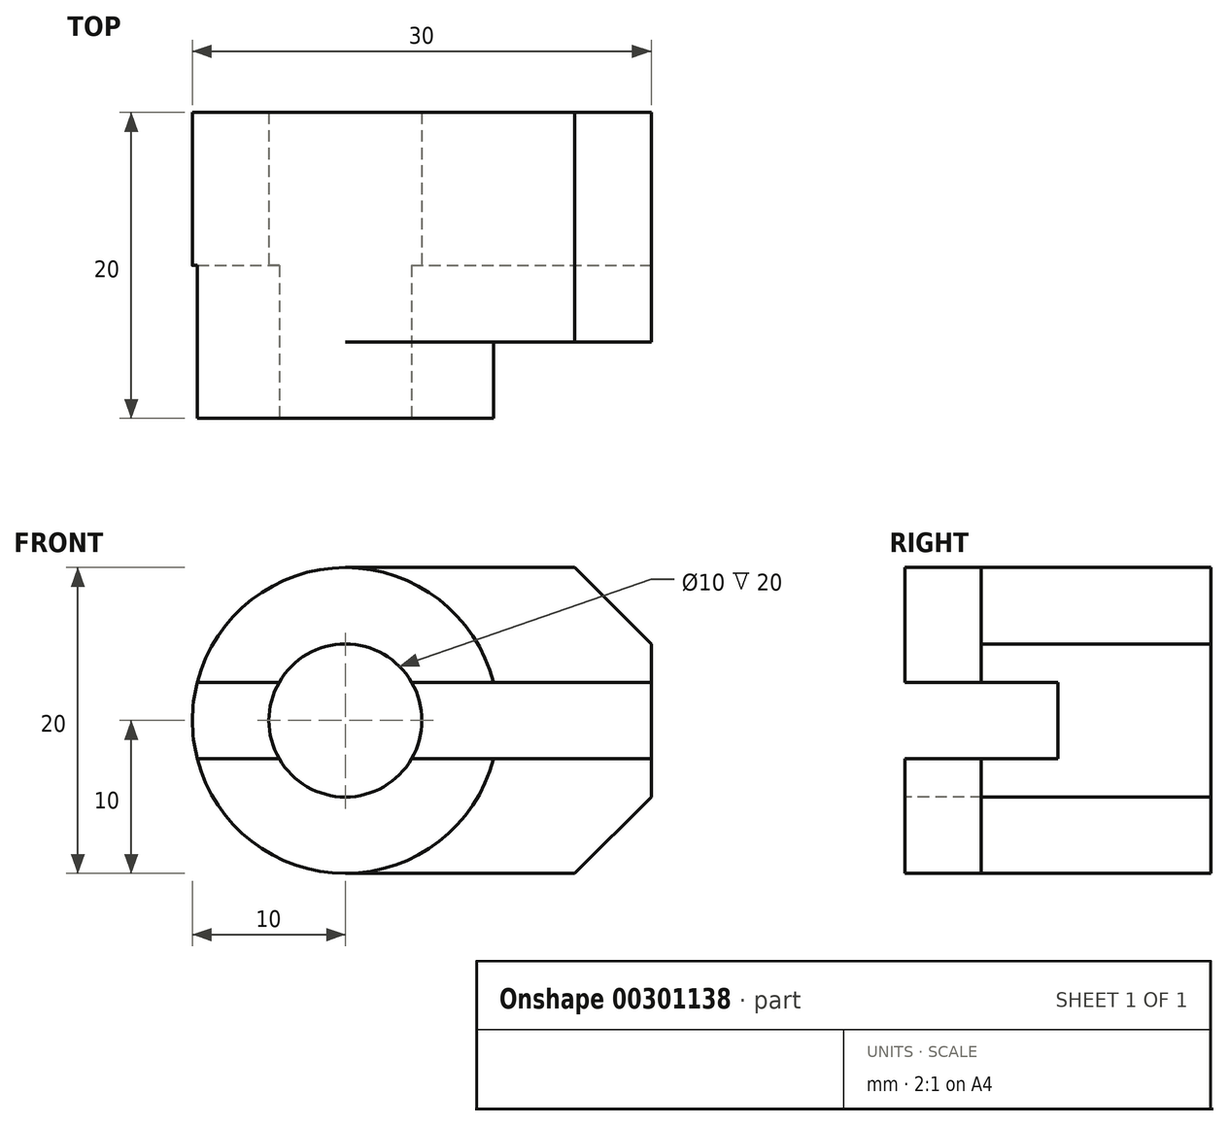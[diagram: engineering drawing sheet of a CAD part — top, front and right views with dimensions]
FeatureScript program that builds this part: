
annotation { "Feature Type Name" : "Feature", "Feature Type Description" : "" }
export const myFeature = defineFeature(function(context is Context, id is Id, definition is map)
    precondition{}
    {
        {
            var Q0;
            Q0=qCreatedBy(makeId("Front.planeOp"),FACE);
            var sketch = newSketch(context, id + "F0", { "sketchPlane" : qUnion([Q0])});
            skCircle(sketch, "E0", {"center": v(0, 0) * mm, "radius": 10 * mm});
            skLineSegment(sketch, "E1", {"start": v(0, 10) * mm, "end": v(15, 10) * mm});
            skLineSegment(sketch, "E2", {"start": v(15, 10) * mm, "end": v(20, 5) * mm});
            skLineSegment(sketch, "E3", {"start": v(20, 5) * mm, "end": v(20, -5) * mm});
            skLineSegment(sketch, "E4", {"start": v(20, -5) * mm, "end": v(15, -10) * mm});
            skLineSegment(sketch, "E5", {"start": v(15, -10) * mm, "end": v(0, -10) * mm});
            skSolve(sketch);
        }
        {
            var Q0;
            {var subQ0=sQuery(id+"F0.wireOp",EDGE,"E0");var subQ1=makeQuery(id+"F0.imprint","INTERSECT",VERTEX,{"derivedFrom":[subQ0,sQuery(id+"F0.wireOp",EDGE,"E1")]});Q0=makeQuery(id+"F0.imprint","IMPRINT",FACE,{"disambiguationData":[TD([[makeQuery(id+"F0.imprint","IMPRINT",EDGE,{"disambiguationData":[TD([[subQ1,-1.0]])],"derivedFrom":subQ0}),1.0]])]});}
            extrude(context, id + "F1", {"entities" : qUnion([Q0]), "depth" : 20 * mm});
        }
        {
            var Q0;
            {var subQ0=sQuery(id+"F0.wireOp",EDGE,"E1");Q0=makeQuery(id+"F0.imprint","IMPRINT",FACE,{"disambiguationData":[TD([[makeQuery(id+"F0.imprint","IMPRINT",EDGE,{"derivedFrom":subQ0}),-1.0]])]});}
            extrude(context, id + "F2", {"entities" : qUnion([Q0]), "operationType" : NewBodyOperationType.ADD, "depth" : 15 * mm});
        }
        {
            var Q0;
            Q0=makeQuery(id+"F1.opExtrude","CAP_FACE",FACE,{"disambiguationData":[OSD([sQuery(id+"F0.wireOp",EDGE,"E0")])],"isStart":false});
            var sketch = newSketch(context, id + "F3", { "sketchPlane" : qUnion([Q0])});
            skCircle(sketch, "E6", {"center": v(0, 0) * mm, "radius": 5 * mm});
            skSolve(sketch);
        }
        {
            var Q0;
            Q0=makeQuery(id+"F3.imprint","IMPRINT",FACE,{"disambiguationData":[TD([[makeQuery(id+"F3.imprint","IMPRINT",EDGE,{"derivedFrom":sQuery(id+"F3.wireOp",EDGE,"E6")}),1.0]])]});
            extrude(context, id + "F4", {"entities" : qUnion([Q0]), "operationType" : NewBodyOperationType.REMOVE, "endBound" : BoundingType.THROUGH_ALL, "oppositeDirection" : true, "depth" : 25 * mm});
        }
        {
            var Q0;
            Q0=makeQuery(id+"F2.opExtrude","SWEPT_FACE",FACE,{"disambiguationData":[OSD([sQuery(id+"F0.wireOp",EDGE,"E3")])]});
            var sketch = newSketch(context, id + "F5", { "sketchPlane" : qUnion([Q0])});
            skLineSegment(sketch, "E7.bottom", {"start": v(-10, 2.5) * mm, "end": v(-20, 2.5) * mm});
            skLineSegment(sketch, "E7.top", {"start": v(-10, -2.5) * mm, "end": v(-20, -2.5) * mm});
            skLineSegment(sketch, "E7.left", {"start": v(-10, 2.5) * mm, "end": v(-10, -2.5) * mm});
            skLineSegment(sketch, "E7.right", {"start": v(-20, 2.5) * mm, "end": v(-20, -2.5) * mm});
            skLineSegment(sketch, "E8", {"start": v(-21.06, 0) * mm, "end": v(0, 0) * mm, "construction": true});
            skSolve(sketch);
        }
        {
            var Q0;
            {var subQ0=sQuery(id+"F5.wireOp",EDGE,"E7.left");Q0=makeQuery(id+"F5.imprint","IMPRINT",FACE,{"disambiguationData":[TD([[makeQuery(id+"F5.imprint","IMPRINT",EDGE,{"derivedFrom":subQ0}),-1.0]])]});}
            var Q1;
            {var subQ0=sQuery(id+"F5.wireOp",EDGE,"E7.right");Q1=makeQuery(id+"F5.imprint","IMPRINT",FACE,{"disambiguationData":[TD([[makeQuery(id+"F5.imprint","IMPRINT",EDGE,{"derivedFrom":subQ0}),1.0]])]});}
            extrude(context, id + "F6", {"entities" : qUnion([Q0, Q1]), "operationType" : NewBodyOperationType.REMOVE, "endBound" : BoundingType.THROUGH_ALL, "oppositeDirection" : true, "depth" : 25 * mm});
        }
    });
